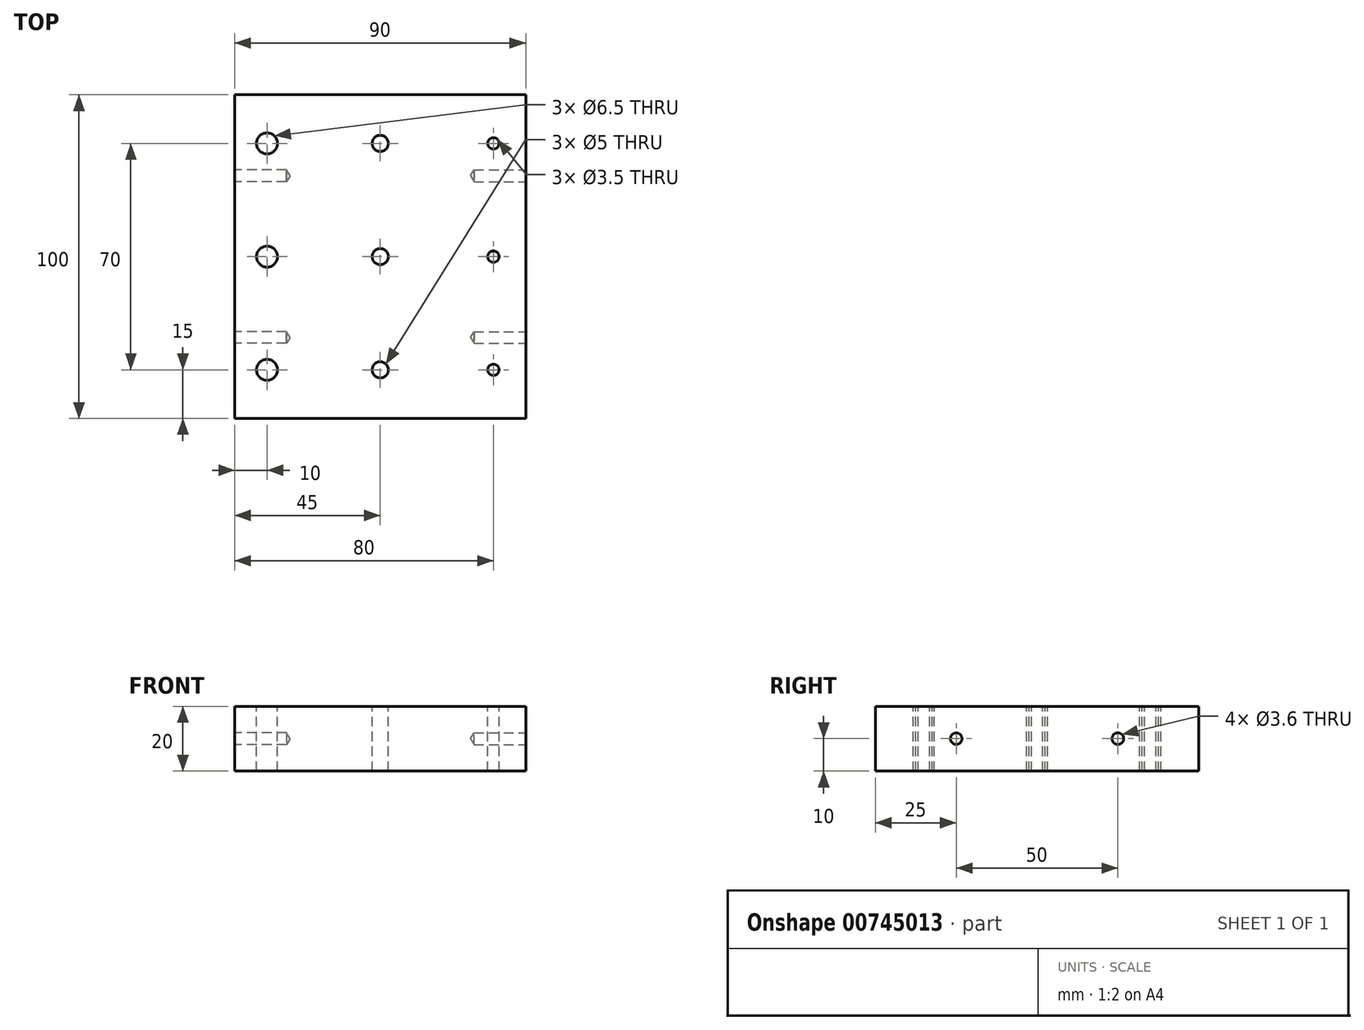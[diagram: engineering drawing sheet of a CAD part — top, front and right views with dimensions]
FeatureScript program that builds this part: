
annotation { "Feature Type Name" : "Feature", "Feature Type Description" : "" }
export const myFeature = defineFeature(function(context is Context, id is Id, definition is map)
    precondition{}
    {
        {
            var Q0;
            Q0=qCreatedBy(makeId("Top.planeOp"),FACE);
            var sketch = newSketch(context, id + "F0", { "sketchPlane" : qUnion([Q0])});
            skLineSegment(sketch, "E0.bottom", {"start": v(45, -50) * mm, "end": v(-45, -50) * mm});
            skLineSegment(sketch, "E0.top", {"start": v(45, 50) * mm, "end": v(-45, 50) * mm});
            skLineSegment(sketch, "E0.left", {"start": v(45, -50) * mm, "end": v(45, 50) * mm});
            skLineSegment(sketch, "E0.right", {"start": v(-45, -50) * mm, "end": v(-45, 50) * mm});
            skPoint(sketch, "E0.middle", {"position": v(0, 0) * mm});
            skPoint(sketch, "E1", {"position": v(-35, 0) * mm});
            skPoint(sketch, "E2", {"position": v(35, 0) * mm});
            skPoint(sketch, "E3.0.1.0", {"position": v(-35, 35) * mm});
            skPoint(sketch, "E3.0.1.1", {"position": v(0, 35) * mm});
            skPoint(sketch, "E3.0.1.2", {"position": v(35, 35) * mm});
            skPoint(sketch, "E3.0.1.3", {"position": v(0, 35) * mm});
            skPoint(sketch, "E3.1.0.0", {"position": v(-35, -35) * mm});
            skPoint(sketch, "E3.1.0.1", {"position": v(0, -35) * mm});
            skPoint(sketch, "E3.1.0.2", {"position": v(35, -35) * mm});
            skPoint(sketch, "E3.1.0.3", {"position": v(0, -35) * mm});
            skLineSegment(sketch, "E3.direction1", {"start": v(-35, 0) * mm, "end": v(-35, -35) * mm, "construction": true});
            skLineSegment(sketch, "E3.direction2", {"start": v(-35, 0) * mm, "end": v(-35, 35) * mm, "construction": true});
            skSolve(sketch);
        }
        {
            var Q0;
            Q0=makeQuery(id+"F0.imprint","IMPRINT",FACE,{"disambiguationData":[TD([[makeQuery(id+"F0.imprint","IMPRINT",EDGE,{"derivedFrom":sQuery(id+"F0.wireOp",EDGE,"E0.bottom")}),-1.0]])]});
            extrude(context, id + "F1", {"entities" : qUnion([Q0]), "oppositeDirection" : true, "depth" : 20 * mm, "offsetDistance" : 25 * mm});
        }
        {
            var Q0;
            Q0=sQuery(id+"F0.wireOp",VERTEX,"E3.0.1.0");
            var Q1;
            Q1=sQuery(id+"F0.wireOp",VERTEX,"E1");
            var Q2;
            Q2=sQuery(id+"F0.wireOp",VERTEX,"E3.1.0.0");
            var Q3;
            Q3=makeQuery(id+"F1.opExtrude","SWEPT_BODY",BODY,{"disambiguationData":[OSD([sQuery(id+"F0.wireOp",EDGE,"E0.bottom"),sQuery(id+"F0.wireOp",EDGE,"E0.top"),sQuery(id+"F0.wireOp",EDGE,"E0.left"),sQuery(id+"F0.wireOp",EDGE,"E0.right")])]});
            hole(context, id + "F2", {"style" : HoleStyle.SIMPLE, "endStyle" : HoleEndStyle.THROUGH, "holeDiameter" : 6.5 * mm, "majorDiameter" : 5 * mm, "isTappedThrough" : true, "tappedDepth" : 6 * mm, "tapClearance" : 3, "locations" : qUnion([Q0, Q1, Q2]), "scope" : qUnion([Q3])});
        }
        {
            var Q0;
            Q0=sQuery(id+"F0.wireOp",VERTEX,"E3.0.1.1");
            var Q1;
            Q1=sQuery(id+"F0.wireOp",VERTEX,"E0.middle");
            var Q2;
            Q2=sQuery(id+"F0.wireOp",VERTEX,"E3.1.0.1");
            var Q3;
            Q3=makeQuery(id+"F1.opExtrude","SWEPT_BODY",BODY,{"disambiguationData":[OSD([sQuery(id+"F0.wireOp",EDGE,"E0.bottom"),sQuery(id+"F0.wireOp",EDGE,"E0.top"),sQuery(id+"F0.wireOp",EDGE,"E0.left"),sQuery(id+"F0.wireOp",EDGE,"E0.right")])]});
            hole(context, id + "F3", {"style" : HoleStyle.SIMPLE, "endStyle" : HoleEndStyle.THROUGH, "holeDiameter" : 5 * mm, "majorDiameter" : 5 * mm, "isTappedThrough" : true, "tappedDepth" : 6 * mm, "tapClearance" : 3, "locations" : qUnion([Q0, Q1, Q2]), "scope" : qUnion([Q3])});
        }
        {
            var Q0;
            Q0=sQuery(id+"F0.wireOp",VERTEX,"E3.0.1.2");
            var Q1;
            Q1=sQuery(id+"F0.wireOp",VERTEX,"E2");
            var Q2;
            Q2=sQuery(id+"F0.wireOp",VERTEX,"E3.1.0.2");
            var Q3;
            Q3=makeQuery(id+"F1.opExtrude","SWEPT_BODY",BODY,{"disambiguationData":[OSD([sQuery(id+"F0.wireOp",EDGE,"E0.bottom"),sQuery(id+"F0.wireOp",EDGE,"E0.top"),sQuery(id+"F0.wireOp",EDGE,"E0.left"),sQuery(id+"F0.wireOp",EDGE,"E0.right")])]});
            hole(context, id + "F4", {"style" : HoleStyle.SIMPLE, "endStyle" : HoleEndStyle.THROUGH, "holeDiameter" : 3.5 * mm, "majorDiameter" : 5 * mm, "isTappedThrough" : true, "tappedDepth" : 6 * mm, "tapClearance" : 3, "locations" : qUnion([Q0, Q1, Q2]), "scope" : qUnion([Q3])});
        }
        {
            var Q0;
            Q0=makeQuery(id+"F1.opExtrude","SWEPT_FACE",FACE,{"disambiguationData":[OSD([sQuery(id+"F0.wireOp",EDGE,"E0.right")])]});
            var sketch = newSketch(context, id + "F5", { "sketchPlane" : qUnion([Q0])});
            skLineSegment(sketch, "E4", {"start": v(-50, -10) * mm, "end": v(50, -10) * mm, "construction": true});
            skPoint(sketch, "E5", {"position": v(-25, -10) * mm});
            skPoint(sketch, "E6", {"position": v(25, -10) * mm});
            skSolve(sketch);
        }
        {
            var Q0;
            Q0=sQuery(id+"F5.wireOp",VERTEX,"E5");
            var Q1;
            Q1=sQuery(id+"F5.wireOp",VERTEX,"E6");
            var Q2;
            Q2=makeQuery(id+"F1.opExtrude","SWEPT_BODY",BODY,{"disambiguationData":[OSD([sQuery(id+"F0.wireOp",EDGE,"E0.bottom"),sQuery(id+"F0.wireOp",EDGE,"E0.top"),sQuery(id+"F0.wireOp",EDGE,"E0.left"),sQuery(id+"F0.wireOp",EDGE,"E0.right")])]});
            hole(context, id + "F6", {"style" : HoleStyle.SIMPLE, "endStyle" : HoleEndStyle.BLIND, "holeDiameter" : 3.6 * mm, "majorDiameter" : 5 * mm, "holeDepth" : 16 * mm, "isTappedThrough" : true, "tappedDepth" : 6 * mm, "tapClearance" : 3, "locations" : qUnion([Q0, Q1]), "scope" : qUnion([Q2])});
        }
        {
            var Q0;
            Q0=makeQuery(id+"F1.opExtrude","SWEPT_FACE",FACE,{"disambiguationData":[OSD([sQuery(id+"F0.wireOp",EDGE,"E0.left")])]});
            var sketch = newSketch(context, id + "F7", { "sketchPlane" : qUnion([Q0])});
            skLineSegment(sketch, "E7", {"start": v(-50, -10) * mm, "end": v(50, -10) * mm, "construction": true});
            skPoint(sketch, "E8", {"position": v(-25, -10) * mm});
            skPoint(sketch, "E9", {"position": v(25, -10) * mm});
            skSolve(sketch);
        }
        {
            var Q0;
            Q0=sQuery(id+"F7.wireOp",VERTEX,"E8");
            var Q1;
            Q1=sQuery(id+"F7.wireOp",VERTEX,"E9");
            var Q2;
            Q2=makeQuery(id+"F1.opExtrude","SWEPT_BODY",BODY,{"disambiguationData":[OSD([sQuery(id+"F0.wireOp",EDGE,"E0.bottom"),sQuery(id+"F0.wireOp",EDGE,"E0.top"),sQuery(id+"F0.wireOp",EDGE,"E0.left"),sQuery(id+"F0.wireOp",EDGE,"E0.right")])]});
            hole(context, id + "F8", {"style" : HoleStyle.SIMPLE, "endStyle" : HoleEndStyle.BLIND, "holeDiameter" : 3.6 * mm, "majorDiameter" : 5 * mm, "holeDepth" : 16 * mm, "isTappedThrough" : true, "tappedDepth" : 6 * mm, "tapClearance" : 3, "locations" : qUnion([Q0, Q1]), "scope" : qUnion([Q2])});
        }
    });
